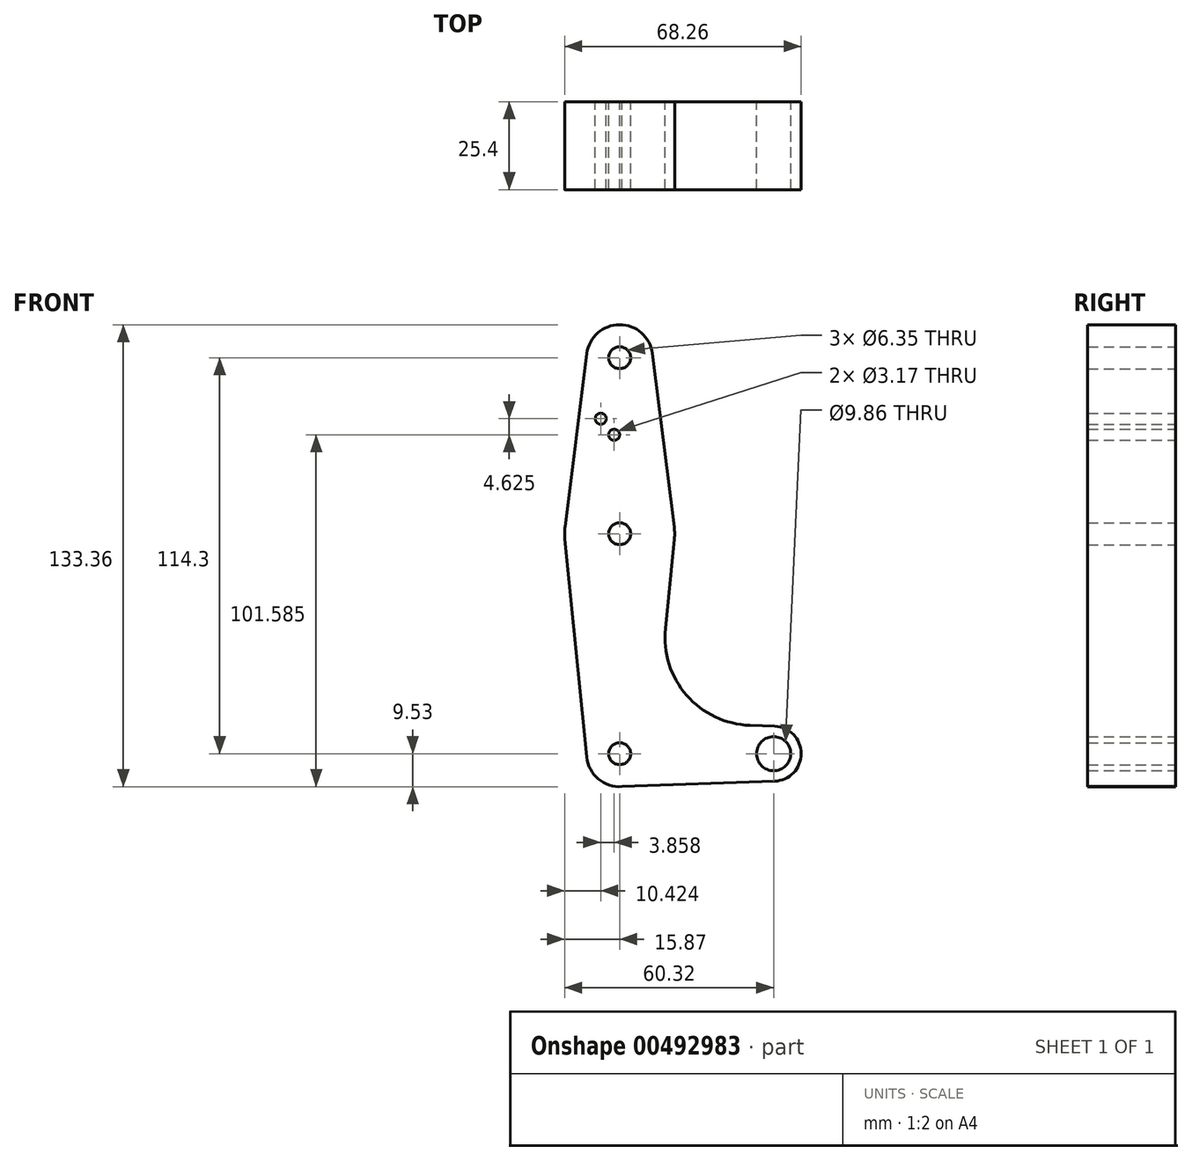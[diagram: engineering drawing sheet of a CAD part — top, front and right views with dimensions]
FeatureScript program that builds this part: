
annotation { "Feature Type Name" : "Feature", "Feature Type Description" : "" }
export const myFeature = defineFeature(function(context is Context, id is Id, definition is map)
    precondition{}
    {
        {
            var Q0;
            Q0=qCreatedBy(makeId("Front.planeOp"),FACE);
            var sketch = newSketch(context, id + "F0", { "sketchPlane" : qUnion([Q0])});
            skLineSegment(sketch, "E0", {"start": v(0, 0) * mm, "end": v(0, 114.3) * mm, "construction": true});
            skLineSegment(sketch, "E1", {"start": v(0, 0) * mm, "end": v(44.45, 0) * mm, "construction": true});
            skCircle(sketch, "E2", {"center": v(44.45, 0) * mm, "radius": 7.94 * mm});
            skCircle(sketch, "E3", {"center": v(0, 0) * mm, "radius": 9.53 * mm});
            skCircle(sketch, "E4", {"center": v(0, 63.5) * mm, "radius": 15.88 * mm});
            skCircle(sketch, "E5", {"center": v(0, 114.3) * mm, "radius": 9.53 * mm});
            skLineSegment(sketch, "E6", {"start": v(-9.45, 115.5) * mm, "end": v(-15.75, 65.48) * mm});
            skLineSegment(sketch, "E7", {"start": v(9.45, 115.5) * mm, "end": v(15.75, 65.48) * mm});
            skLineSegment(sketch, "E8", {"start": v(37.57, 8.19) * mm, "end": v(44.73, 7.93) * mm});
            skLineSegment(sketch, "E9", {"start": v(0, -9.53) * mm, "end": v(44.73, -7.93) * mm});
            skCircle(sketch, "E10", {"center": v(-1.59, 92.05) * mm, "radius": 1.59 * mm});
            skLineSegment(sketch, "E11", {"start": v(15.8, 61.91) * mm, "end": v(13.2, 36.11) * mm});
            skLineSegment(sketch, "E12", {"start": v(-15.8, 61.91) * mm, "end": v(-9.48, -0.95) * mm});
            skCircle(sketch, "E13", {"center": v(-5.45, 96.68) * mm, "radius": 1.59 * mm});
            skCircle(sketch, "E14", {"center": v(0, 114.3) * mm, "radius": 3.18 * mm});
            skCircle(sketch, "E15", {"center": v(0, 63.5) * mm, "radius": 3.18 * mm});
            skCircle(sketch, "E16", {"center": v(0, 0) * mm, "radius": 3.18 * mm});
            skCircle(sketch, "E17", {"center": v(44.45, 0) * mm, "radius": 4.93 * mm});
            skArc(sketch, "E18.filletArc", {"start": v(13.2, 36.11) * mm, "mid": v(19.34, 16.87) * mm, "end": v(37.57, 8.19) * mm});
            skSolve(sketch);
        }
        {
            var Q0;
            Q0 = qSketchRegion(id + "F0", true);
            extrude(context, id + "F1", {"entities" : qUnion([Q0]), "depth" : 25.4 * mm});
        }
    });
